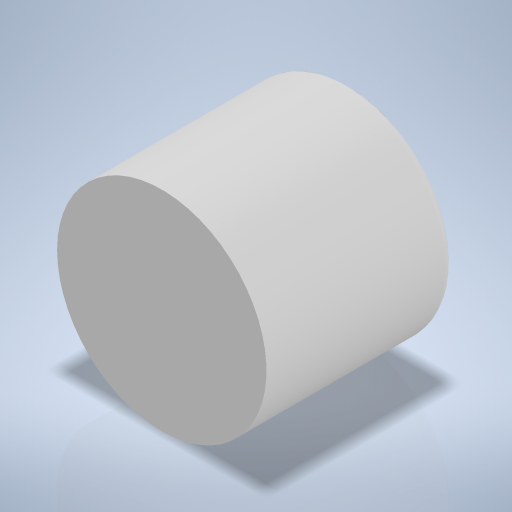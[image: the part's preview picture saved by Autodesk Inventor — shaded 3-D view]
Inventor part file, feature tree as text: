
AUTODESK INVENTOR PART (.ipt)
format: ipt  version: 2024 (Build 280153000, 153)  size: 215,552 bytes
history: native  units: mm
features: extrude x1, fillet x1, sketch x1
ambient origin geometry x8: Origin, YZ Plane, XZ Plane, XY Plane, X Axis, Y Axis, Z Axis, Center Point
bodies: Volumenkörper1 (feature_tree)
feature tree (3):
  extrude  "Extrusion1"  Depth=9.0mm TaperAngle=0.0deg
  fillet  "Rundung1"  Radius=0.5mm
  sketch  "Skizze1"  dims[d0=10.0mm d1=9.0mm d2=0.0mm d3=0.5mm]
